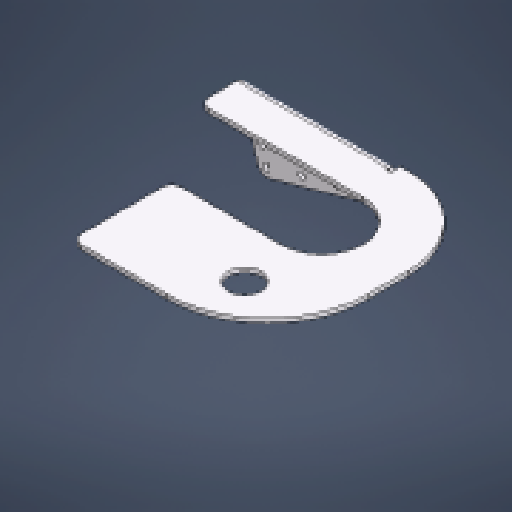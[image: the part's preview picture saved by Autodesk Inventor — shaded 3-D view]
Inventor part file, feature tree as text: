
AUTODESK INVENTOR PART (.ipt)
format: ipt  version: 2024.3 (Build 283343000, 343)  size: 368,128 bytes
history: native  units: mm (DEFAULTED — no unit token found)
features: other x4, sketch x4, sheet_metal_op x3, hole x2, chamfer x2, projected_geometry x1
ambient origin geometry x8: Origin, YZ Plane, XZ Plane, XY Plane, X Axis, Y Axis, Z Axis, Center Point
bodies: Solid1 (feature_tree)
feature tree (16):
  sheet_metal_op  "Face1"
  sheet_metal_op  "Face2"
  hole  "Hole1"  [1 undecoded]
  hole  "Hole2"  [1 undecoded]
  other  "Corner Chamfer1"
  chamfer  "Corner Round1"
  chamfer  "Corner Round2"
  sketch  "Sketch2"  dims[d0=31.75mm d1=73.025mm]
  other  "Plate1"
  sketch  "Sketch3"  dims[d2=3.048mm d4=2.792527mm]
  other  "Plate2"
  sheet_metal_op  "Bend1"
  sketch  "Sketch4"  dims[d6=2.286mm]
  sketch  "Sketch5"  dims[d7=3.048mm d8=1.524mm d9=6.096mm d10=4.572mm d11=41.29024mm d12=28.575mm d13=76.2mm d14=69.85mm d15=101.6mm d17=23.5458mm d18=19.05mm d19=9.525mm d20=6.35mm d21=14.3117mm d22=3.048mm d23=20.594885mm d24=85.725mm d25=34.925mm d26=69.85mm d27=6.35mm d28=6.35mm d29=50.8mm d30=15.875mm d31=6.35mm d32=45.0deg d33=6.35mm d34=12.7mm d35=12.7mm d36=6.35mm d37=6.35mm d38=30.0mm d40=25.4mm d41=10.0mm d43=25.4mm d45=5.1054mm d46=19.05mm d47=9.525mm d48=4.826mm d49=14.3117mm d50=25.4mm d51=20.594885mm]
  projected_geometry  "Projected Loop1"
  other  "Definition1"
note: 2 required parameter values undecoded (feature->parameter linkage not recoverable at this tier; creation-order binding heuristic only, values carry confidence <= 0.55)
